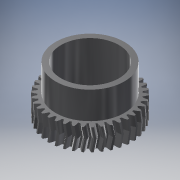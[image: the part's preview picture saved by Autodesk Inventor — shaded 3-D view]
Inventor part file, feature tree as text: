
AUTODESK INVENTOR PART (.ipt)
format: ipt  version: 2018 (Build 220112000, 112)  size: 907,776 bytes
history: native  units: mm (DEFAULTED — no unit token found)
features: other x4, sketch x4, extrude x3, plane x3, mirror x1
ambient origin geometry x8: Origin, YZ Plane, XZ Plane, XY Plane, X Axis, Y Axis, Z Axis, Center Point
bodies: Solid1 (feature_tree)
feature tree (15):
  other  "Ground_Tracker_ElevationGear"
  extrude  "Extrusion1"  Depth=8.0mm TaperAngle=0.0deg
  plane  "Work Plane2"
  plane  "Work Plane8"
  plane  "Work Plane9"
  other  "Spur Gear"
  mirror  "Mirror1"
  extrude  "Extrusion2"  Depth=10.0mm TaperAngle=0.0deg
  extrude  "Extrusion3"  Depth=0.826735mm TaperAngle=0.0deg
  sketch  "Sketch1"  dims[d0=61.312491mm d1=8.0mm d2=0.0mm]
  sketch  "Sketch2"  dims[d3=58.140596mm d4=10.0mm d5=0.0mm]
  other  "Srf1"
  sketch  "Sketch3"  dims[d16=48.195494mm d17=0.0mm d34=0.826735mm]
  sketch  "Sketch4"  dims[d39=0.0mm d41=0.0mm d43=48.195494mm d46=48.195494mm d47=0.0mm d48=0.0mm d49=42.418mm d50=10.0mm d51=0.0mm d52=4.0mm d53=20.0mm d54=0.0mm]
  other  "Pitch Diameter"
